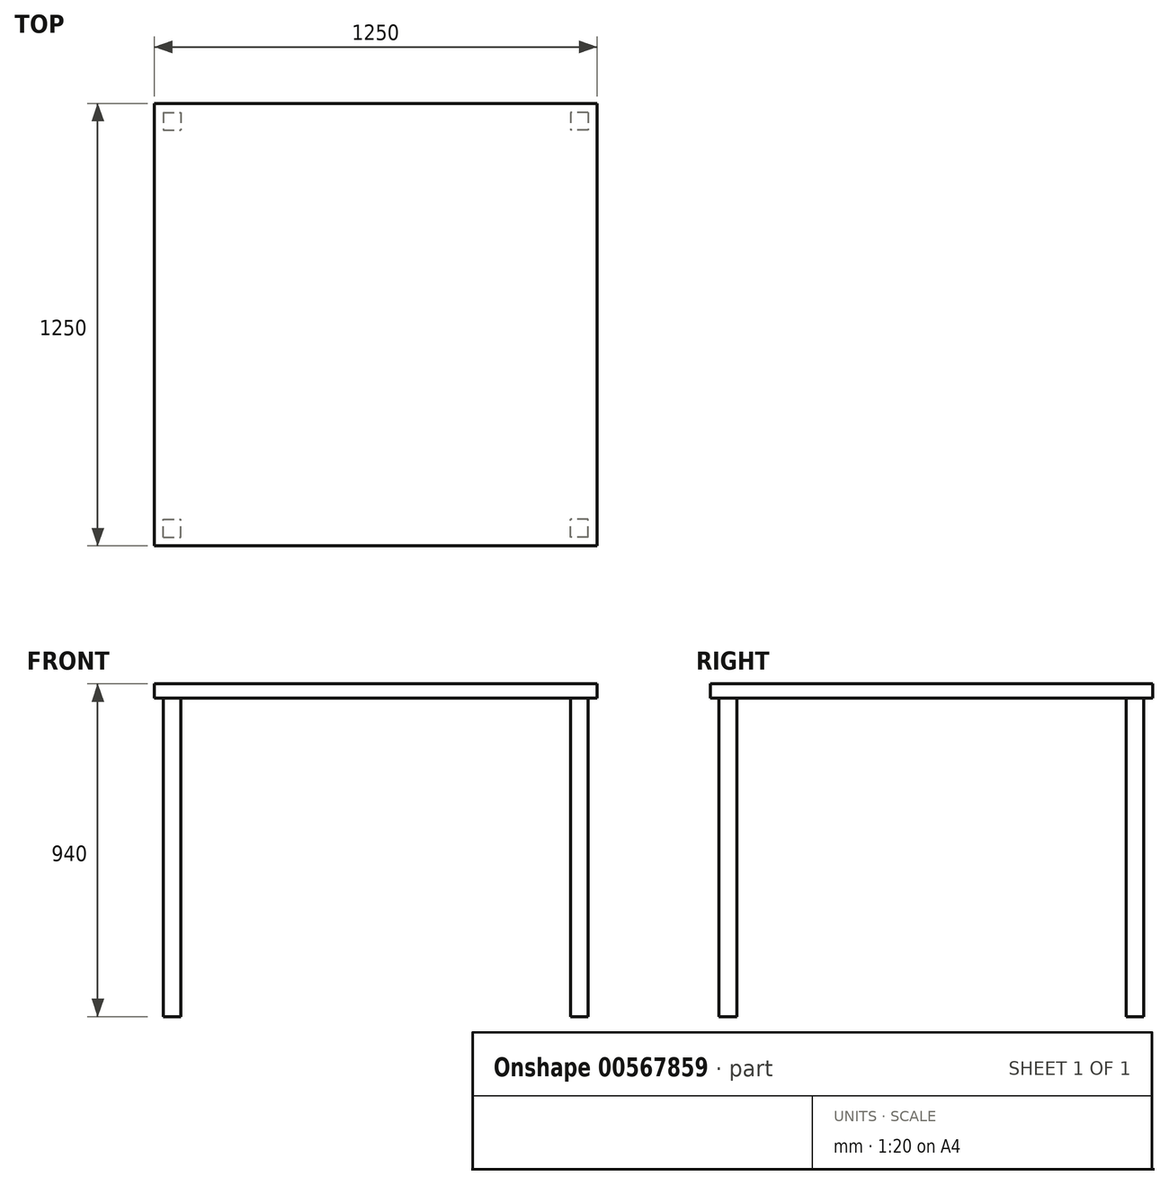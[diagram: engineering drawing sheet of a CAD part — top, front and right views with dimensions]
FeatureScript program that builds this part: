
annotation { "Feature Type Name" : "Feature", "Feature Type Description" : "" }
export const myFeature = defineFeature(function(context is Context, id is Id, definition is map)
    precondition{}
    {
        {
            var Q0;
            Q0=qCreatedBy(makeId("Top.planeOp"),FACE);
            var sketch = newSketch(context, id + "F0", { "sketchPlane" : qUnion([Q0])});
            skLineSegment(sketch, "E0.bottom", {"start": v(-600, 600) * mm, "end": v(-550, 600) * mm});
            skLineSegment(sketch, "E0.top", {"start": v(-600, 550) * mm, "end": v(-550, 550) * mm});
            skLineSegment(sketch, "E0.left", {"start": v(-600, 600) * mm, "end": v(-600, 550) * mm});
            skLineSegment(sketch, "E0.right", {"start": v(-550, 600) * mm, "end": v(-550, 550) * mm});
            skLineSegment(sketch, "E1.MirrorCS", {"start": v(550, 600) * mm, "end": v(550, 550) * mm});
            skLineSegment(sketch, "E2.MirrorCS", {"start": v(600, 600) * mm, "end": v(600, 550) * mm});
            skLineSegment(sketch, "E3.MirrorCS", {"start": v(600, 600) * mm, "end": v(550, 600) * mm});
            skLineSegment(sketch, "E4.MirrorCS", {"start": v(600, 550) * mm, "end": v(550, 550) * mm});
            skLineSegment(sketch, "E5.MirrorCS", {"start": v(600, -600) * mm, "end": v(600, -550) * mm});
            skLineSegment(sketch, "E6.MirrorCS", {"start": v(550, -600) * mm, "end": v(550, -550) * mm});
            skLineSegment(sketch, "E7.MirrorCS", {"start": v(-550, -600) * mm, "end": v(-550, -550) * mm});
            skLineSegment(sketch, "E8.MirrorCS", {"start": v(-600, -600) * mm, "end": v(-600, -550) * mm});
            skLineSegment(sketch, "E9.MirrorCS", {"start": v(600, -600) * mm, "end": v(550, -600) * mm});
            skLineSegment(sketch, "E10.MirrorCS", {"start": v(-600, -550) * mm, "end": v(-550, -550) * mm});
            skLineSegment(sketch, "E11.MirrorCS", {"start": v(-600, -600) * mm, "end": v(-550, -600) * mm});
            skLineSegment(sketch, "E12.MirrorCS", {"start": v(600, -550) * mm, "end": v(550, -550) * mm});
            skSolve(sketch);
        }
        {
            var Q0;
            Q0 = qSketchRegion(id + "F0", true);
            extrude(context, id + "F1", {"entities" : qUnion([Q0]), "depth" : 900 * mm, "offsetDistance" : 25 * mm});
        }
        {
            var Q0;
            Q0=makeQuery(id+"F1.opExtrude","CAP_FACE",FACE,{"disambiguationData":[OSD([sQuery(id+"F0.wireOp",EDGE,"E7.MirrorCS"),sQuery(id+"F0.wireOp",EDGE,"E8.MirrorCS"),sQuery(id+"F0.wireOp",EDGE,"E10.MirrorCS"),sQuery(id+"F0.wireOp",EDGE,"E11.MirrorCS")])],"isStart":false});
            var sketch = newSketch(context, id + "F2", { "sketchPlane" : qUnion([Q0])});
            skLineSegment(sketch, "E13.bottom", {"start": v(-625, 625) * mm, "end": v(625, 625) * mm});
            skLineSegment(sketch, "E13.top", {"start": v(-625, -625) * mm, "end": v(625, -625) * mm});
            skLineSegment(sketch, "E13.left", {"start": v(-625, 625) * mm, "end": v(-625, -625) * mm});
            skLineSegment(sketch, "E13.right", {"start": v(625, 625) * mm, "end": v(625, -625) * mm});
            skPoint(sketch, "E14", {"position": v(-625, 0) * mm});
            skPoint(sketch, "E15", {"position": v(0, 625) * mm});
            skSolve(sketch);
        }
        {
            var Q0;
            Q0 = qSketchRegion(id + "F2", true);
            extrude(context, id + "F3", {"entities" : qUnion([Q0]), "operationType" : NewBodyOperationType.ADD, "depth" : 40 * mm, "offsetDistance" : 25 * mm});
        }
    });
